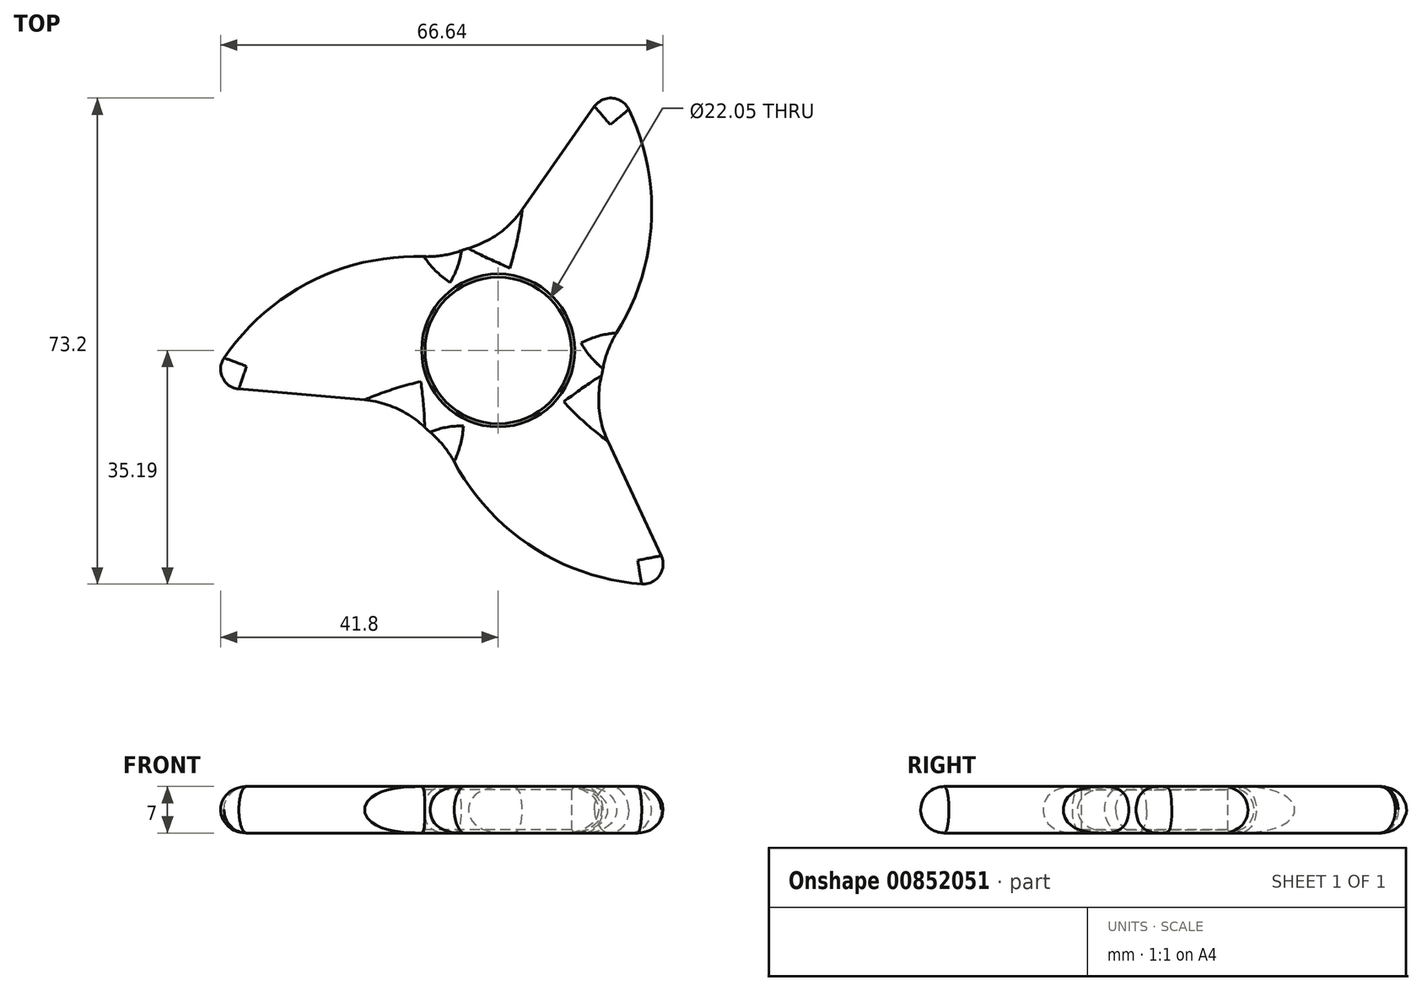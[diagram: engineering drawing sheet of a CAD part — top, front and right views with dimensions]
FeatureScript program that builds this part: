
annotation { "Feature Type Name" : "Feature", "Feature Type Description" : "" }
export const myFeature = defineFeature(function(context is Context, id is Id, definition is map)
    precondition{}
    {
        {
            var Q0;
            Q0=qCreatedBy(makeId("Top.planeOp"),FACE);
            var sketch = newSketch(context, id + "F0", { "sketchPlane" : qUnion([Q0])});
            skCircle(sketch, "E0", {"center": v(0, 0) * mm, "radius": 11.03 * mm});
            skCircle(sketch, "E1", {"center": v(0, 0) * mm, "radius": 16.03 * mm});
            skLineSegment(sketch, "E2", {"start": v(0, 16.02) * mm, "end": v(14.5, 36.73) * mm});
            skArc(sketch, "E3", {"start": v(16.03, 0) * mm, "mid": v(22.95, 17.64) * mm, "end": v(19.66, 36.31) * mm});
            skPoint(sketch, "E4.visualSharp", {"position": v(17.2, 40.6) * mm});
            skArc(sketch, "E4.filletArc", {"start": v(19.66, 36.31) * mm, "mid": v(17.2, 38) * mm, "end": v(14.5, 36.73) * mm});
            skSolve(sketch);
        }
        {
            var Q0;
            Q0 = qSketchRegion(id + "F0", true);
            extrude(context, id + "F1", {"entities" : qUnion([Q0]), "depth" : 7 * mm, "offsetDistance" : 25 * mm});
        }
        {
            var Q0;
            Q0=qCreatedBy(makeId("Right.planeOp"),FACE);
            var sketch = newSketch(context, id + "F2", { "sketchPlane" : qUnion([Q0])});
            skLineSegment(sketch, "E5", {"start": v(0, 0) * mm, "end": v(0, -17.5) * mm});
            skSolve(sketch);
        }
        {
            var Q0;
            Q0=makeQuery(id+"F1.opExtrude","CAP_EDGE",EDGE,{"disambiguationData":[OSD([sQuery(id+"F0.wireOp",EDGE,"E3")])],"isStart":false});
            var Q1;
            Q1=makeQuery(id+"F1.opExtrude","CAP_EDGE",EDGE,{"disambiguationData":[OSD([sQuery(id+"F0.wireOp",EDGE,"E3")])],"isStart":true});
            var Q2;
            Q2=makeQuery(id+"F1.opExtrude","CAP_EDGE",EDGE,{"disambiguationData":[OSD([sQuery(id+"F0.wireOp",EDGE,"E1")])],"isStart":true});
            var Q3;
            Q3=makeQuery(id+"F1.opExtrude","CAP_EDGE",EDGE,{"disambiguationData":[OSD([sQuery(id+"F0.wireOp",EDGE,"E1")])],"isStart":false});
            fillet(context, id + "F3", {"entities" : qUnion([Q0, Q1, Q2, Q3]), "radius" : 3.5 * mm, "tangentPropagation" : true, "allowEdgeOverflow" : false});
        }
        {
            var Q0;
            Q0=makeQuery(id+"F1.opExtrude","SWEPT_BODY",BODY,{"disambiguationData":[OSD([sQuery(id+"F0.wireOp",EDGE,"E0"),sQuery(id+"F0.wireOp",EDGE,"E1"),sQuery(id+"F0.wireOp",EDGE,"E2"),sQuery(id+"F0.wireOp",EDGE,"E3"),sQuery(id+"F0.wireOp",EDGE,"E4.filletArc")])]});
            var Q1;
            Q1=sQuery(id+"F2.wireOp",EDGE,"E5");
            circularPattern(context, id + "F4", {"entities" : qUnion([Q0]), "axis" : qUnion([Q1]), "angle" : 360 * degree, "instanceCount" : 3, "equalSpace" : true});
        }
        {
            var Q0;
            Q0=makeQuery(id+"F1.opExtrude","SWEPT_BODY",BODY,{"disambiguationData":[OSD([sQuery(id+"F0.wireOp",EDGE,"E0"),sQuery(id+"F0.wireOp",EDGE,"E1"),sQuery(id+"F0.wireOp",EDGE,"E2"),sQuery(id+"F0.wireOp",EDGE,"E3"),sQuery(id+"F0.wireOp",EDGE,"E4.filletArc")])]});
            var Q1;
            Q1=makeQuery(id+"F4.opPattern","COPY",BODY,{"derivedFrom":makeQuery(id+"F1.opExtrude","SWEPT_BODY",BODY,{"disambiguationData":[OSD([sQuery(id+"F0.wireOp",EDGE,"E0"),sQuery(id+"F0.wireOp",EDGE,"E1"),sQuery(id+"F0.wireOp",EDGE,"E2"),sQuery(id+"F0.wireOp",EDGE,"E3"),sQuery(id+"F0.wireOp",EDGE,"E4.filletArc")])]}),"instanceName":"1"});
            var Q2;
            Q2=makeQuery(id+"F4.opPattern","COPY",BODY,{"derivedFrom":makeQuery(id+"F1.opExtrude","SWEPT_BODY",BODY,{"disambiguationData":[OSD([sQuery(id+"F0.wireOp",EDGE,"E0"),sQuery(id+"F0.wireOp",EDGE,"E1"),sQuery(id+"F0.wireOp",EDGE,"E2"),sQuery(id+"F0.wireOp",EDGE,"E3"),sQuery(id+"F0.wireOp",EDGE,"E4.filletArc")])]}),"instanceName":"2"});
            booleanBodies(context, id + "F5", {"operationType" : BooleanOperationType.UNION, "tools" : qUnion([Q0, Q1, Q2])});
        }
        {
            var Q0;
            {var subQ0=sQuery(id+"F0.wireOp",EDGE,"E2");var subQ1=sQuery(id+"F0.wireOp",EDGE,"E1");Q0=makeQuery(id+"F5.opBoolean","MERGE",EDGE,{"derivedFrom":[makeQuery(id+"F3.opFillet","BLEND_EDGE",EDGE,{"blendedFrom":[makeQuery(id+"F1.opExtrude","CAP_EDGE",EDGE,{"disambiguationData":[OSD([subQ1])],"isStart":true}),makeQuery(id+"F1.opExtrude","CAP_EDGE",EDGE,{"disambiguationData":[OSD([subQ0])],"isStart":true})],"blendedInto":[]}),makeQuery(id+"F3.opFillet","BLEND_EDGE",EDGE,{"blendedFrom":[makeQuery(id+"F1.opExtrude","CAP_EDGE",EDGE,{"disambiguationData":[OSD([subQ1])],"isStart":false}),makeQuery(id+"F1.opExtrude","CAP_EDGE",EDGE,{"disambiguationData":[OSD([subQ0])],"isStart":false})],"blendedInto":[]})]});}
            var Q1;
            {var subQ0=sQuery(id+"F0.wireOp",EDGE,"E3");var subQ1=sQuery(id+"F0.wireOp",EDGE,"E1");Q1=makeQuery(id+"F5.opBoolean","MERGE",EDGE,{"derivedFrom":[makeQuery(id+"F4.opPattern","COPY",EDGE,{"derivedFrom":makeQuery(id+"F3.opFillet","BLEND_EDGE",EDGE,{"blendedFrom":[makeQuery(id+"F1.opExtrude","CAP_EDGE",EDGE,{"disambiguationData":[OSD([subQ1])],"isStart":true}),makeQuery(id+"F1.opExtrude","CAP_EDGE",EDGE,{"disambiguationData":[OSD([subQ0])],"isStart":true})],"blendedInto":[]}),"instanceName":"2"}),makeQuery(id+"F4.opPattern","COPY",EDGE,{"derivedFrom":makeQuery(id+"F3.opFillet","BLEND_EDGE",EDGE,{"blendedFrom":[makeQuery(id+"F1.opExtrude","CAP_EDGE",EDGE,{"disambiguationData":[OSD([subQ1])],"isStart":false}),makeQuery(id+"F1.opExtrude","CAP_EDGE",EDGE,{"disambiguationData":[OSD([subQ0])],"isStart":false})],"blendedInto":[]}),"instanceName":"2"})]});}
            var Q2;
            {var subQ0=sQuery(id+"F0.wireOp",EDGE,"E3");var subQ1=sQuery(id+"F0.wireOp",EDGE,"E1");Q2=makeQuery(id+"F5.opBoolean","MERGE",EDGE,{"derivedFrom":[makeQuery(id+"F3.opFillet","BLEND_EDGE",EDGE,{"blendedFrom":[makeQuery(id+"F1.opExtrude","CAP_EDGE",EDGE,{"disambiguationData":[OSD([subQ1])],"isStart":true}),makeQuery(id+"F1.opExtrude","CAP_EDGE",EDGE,{"disambiguationData":[OSD([subQ0])],"isStart":true})],"blendedInto":[]}),makeQuery(id+"F3.opFillet","BLEND_EDGE",EDGE,{"blendedFrom":[makeQuery(id+"F1.opExtrude","CAP_EDGE",EDGE,{"disambiguationData":[OSD([subQ1])],"isStart":false}),makeQuery(id+"F1.opExtrude","CAP_EDGE",EDGE,{"disambiguationData":[OSD([subQ0])],"isStart":false})],"blendedInto":[]})]});}
            var Q3;
            {var subQ0=sQuery(id+"F0.wireOp",EDGE,"E2");var subQ1=sQuery(id+"F0.wireOp",EDGE,"E1");Q3=makeQuery(id+"F5.opBoolean","MERGE",EDGE,{"derivedFrom":[makeQuery(id+"F4.opPattern","COPY",EDGE,{"derivedFrom":makeQuery(id+"F3.opFillet","BLEND_EDGE",EDGE,{"blendedFrom":[makeQuery(id+"F1.opExtrude","CAP_EDGE",EDGE,{"disambiguationData":[OSD([subQ1])],"isStart":true}),makeQuery(id+"F1.opExtrude","CAP_EDGE",EDGE,{"disambiguationData":[OSD([subQ0])],"isStart":true})],"blendedInto":[]}),"instanceName":"1"}),makeQuery(id+"F4.opPattern","COPY",EDGE,{"derivedFrom":makeQuery(id+"F3.opFillet","BLEND_EDGE",EDGE,{"blendedFrom":[makeQuery(id+"F1.opExtrude","CAP_EDGE",EDGE,{"disambiguationData":[OSD([subQ1])],"isStart":false}),makeQuery(id+"F1.opExtrude","CAP_EDGE",EDGE,{"disambiguationData":[OSD([subQ0])],"isStart":false})],"blendedInto":[]}),"instanceName":"1"})]});}
            var Q4;
            {var subQ0=sQuery(id+"F0.wireOp",EDGE,"E3");var subQ1=sQuery(id+"F0.wireOp",EDGE,"E1");Q4=makeQuery(id+"F5.opBoolean","MERGE",EDGE,{"derivedFrom":[makeQuery(id+"F4.opPattern","COPY",EDGE,{"derivedFrom":makeQuery(id+"F3.opFillet","BLEND_EDGE",EDGE,{"blendedFrom":[makeQuery(id+"F1.opExtrude","CAP_EDGE",EDGE,{"disambiguationData":[OSD([subQ1])],"isStart":true}),makeQuery(id+"F1.opExtrude","CAP_EDGE",EDGE,{"disambiguationData":[OSD([subQ0])],"isStart":true})],"blendedInto":[]}),"instanceName":"1"}),makeQuery(id+"F4.opPattern","COPY",EDGE,{"derivedFrom":makeQuery(id+"F3.opFillet","BLEND_EDGE",EDGE,{"blendedFrom":[makeQuery(id+"F1.opExtrude","CAP_EDGE",EDGE,{"disambiguationData":[OSD([subQ1])],"isStart":false}),makeQuery(id+"F1.opExtrude","CAP_EDGE",EDGE,{"disambiguationData":[OSD([subQ0])],"isStart":false})],"blendedInto":[]}),"instanceName":"1"})]});}
            var Q5;
            {var subQ0=sQuery(id+"F0.wireOp",EDGE,"E2");var subQ1=sQuery(id+"F0.wireOp",EDGE,"E1");Q5=makeQuery(id+"F5.opBoolean","MERGE",EDGE,{"derivedFrom":[makeQuery(id+"F4.opPattern","COPY",EDGE,{"derivedFrom":makeQuery(id+"F3.opFillet","BLEND_EDGE",EDGE,{"blendedFrom":[makeQuery(id+"F1.opExtrude","CAP_EDGE",EDGE,{"disambiguationData":[OSD([subQ1])],"isStart":true}),makeQuery(id+"F1.opExtrude","CAP_EDGE",EDGE,{"disambiguationData":[OSD([subQ0])],"isStart":true})],"blendedInto":[]}),"instanceName":"2"}),makeQuery(id+"F4.opPattern","COPY",EDGE,{"derivedFrom":makeQuery(id+"F3.opFillet","BLEND_EDGE",EDGE,{"blendedFrom":[makeQuery(id+"F1.opExtrude","CAP_EDGE",EDGE,{"disambiguationData":[OSD([subQ1])],"isStart":false}),makeQuery(id+"F1.opExtrude","CAP_EDGE",EDGE,{"disambiguationData":[OSD([subQ0])],"isStart":false})],"blendedInto":[]}),"instanceName":"2"})]});}
            fillet(context, id + "F6", {"entities" : qUnion([Q0, Q1, Q2, Q3, Q4, Q5]), "radius" : 15 * mm, "tangentPropagation" : true, "allowEdgeOverflow" : false});
        }
        {
            var Q0;
            Q0=makeQuery(id+"F1.opExtrude","CAP_EDGE",EDGE,{"disambiguationData":[OSD([sQuery(id+"F0.wireOp",EDGE,"E0")])],"isStart":false});
            var Q1;
            Q1=makeQuery(id+"F1.opExtrude","CAP_EDGE",EDGE,{"disambiguationData":[OSD([sQuery(id+"F0.wireOp",EDGE,"E0")])],"isStart":true});
            chamfer(context, id + "F7", {"entities" : qUnion([Q0, Q1]), "width" : .5 * mm, "tangentPropagation" : true});
        }
    });
